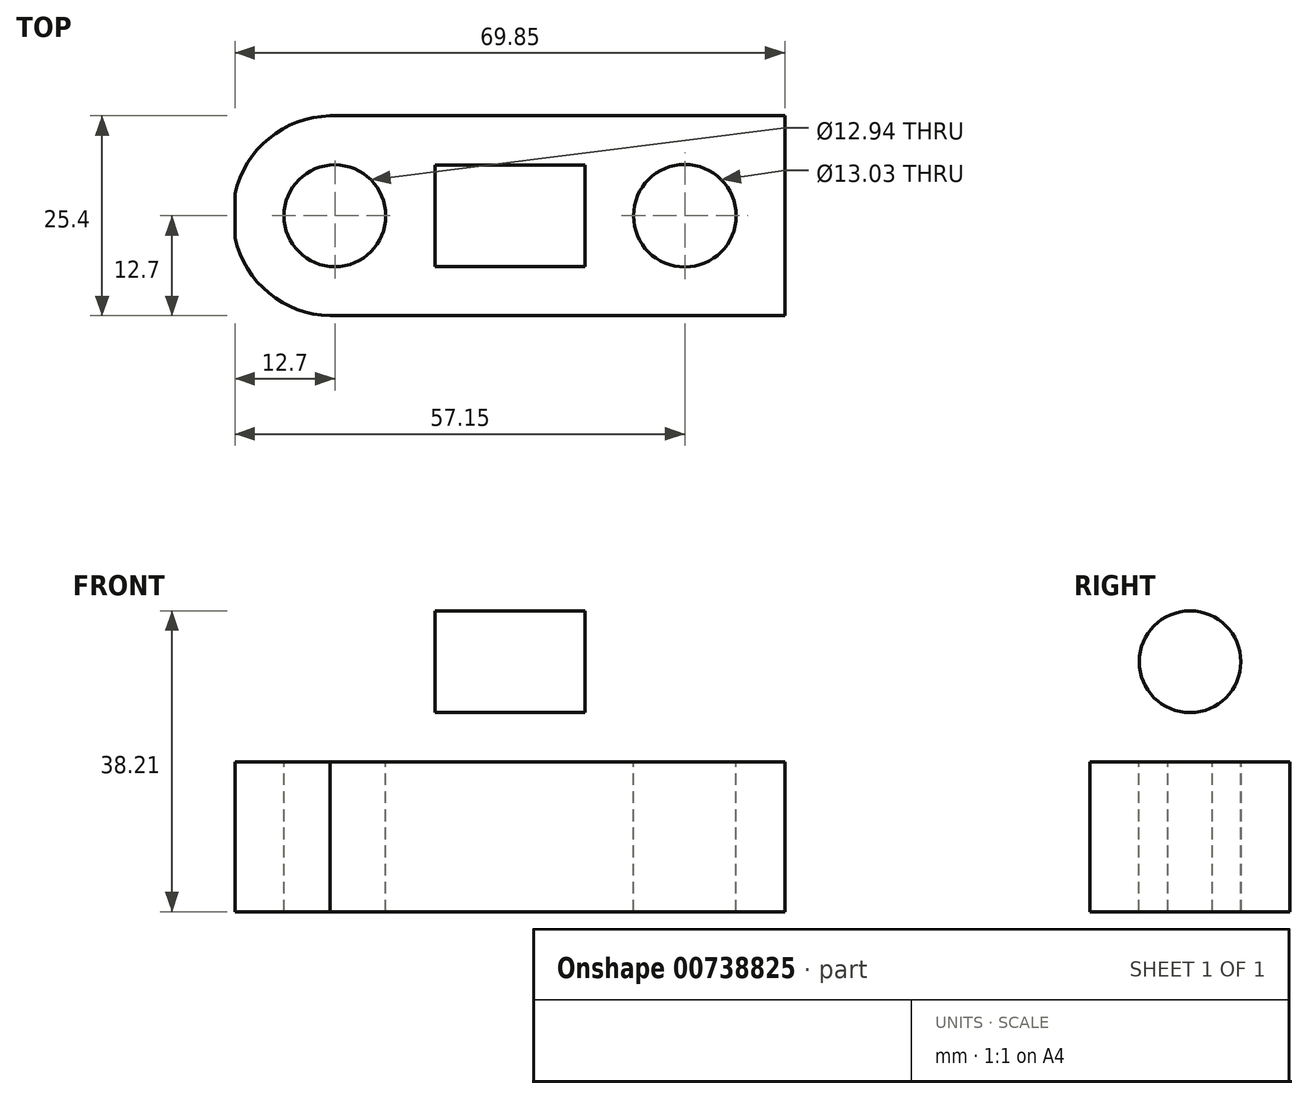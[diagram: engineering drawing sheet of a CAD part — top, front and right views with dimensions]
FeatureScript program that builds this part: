
annotation { "Feature Type Name" : "Feature", "Feature Type Description" : "" }
export const myFeature = defineFeature(function(context is Context, id is Id, definition is map)
    precondition{}
    {
        {
            var Q0;
            Q0=qCreatedBy(makeId("Front.planeOp"),FACE);
            var sketch = newSketch(context, id + "F0", { "sketchPlane" : qUnion([Q0])});
            skLineSegment(sketch, "E0", {"start": v(0, 0) * mm, "end": v(0, 44.45) * mm});
            skLineSegment(sketch, "E1", {"start": v(0, 44.45) * mm, "end": v(69.85, 44.45) * mm});
            skLineSegment(sketch, "E2", {"start": v(69.85, 44.45) * mm, "end": v(69.85, 0) * mm});
            skLineSegment(sketch, "E3", {"start": v(69.85, 0) * mm, "end": v(0, 0) * mm});
            skSolve(sketch);
        }
        {
            var Q0;
            Q0 = qSketchRegion(id + "F0", true);
            extrude(context, id + "F1", {"entities" : qUnion([Q0]), "depth" : 25.4 * mm, "offsetDistance" : 25.4 * mm});
        }
        {
            var Q0;
            Q0=makeQuery(id+"F1.opExtrude","SWEPT_FACE",FACE,{"disambiguationData":[OSD([sQuery(id+"F0.wireOp",EDGE,"E1")])]});
            var sketch = newSketch(context, id + "F2", { "sketchPlane" : qUnion([Q0])});
            skLineSegment(sketch, "E4", {"start": v(25.4, 0) * mm, "end": v(25.4, -25.4) * mm});
            skLineSegment(sketch, "E5", {"start": v(44.45, 0) * mm, "end": v(44.45, -25.4) * mm});
            skSolve(sketch);
        }
        {
            var Q0;
            {var subQ0=sQuery(id+"F2.wireOp",EDGE,"E4");Q0=makeQuery(id+"F2.imprint","IMPRINT",FACE,{"disambiguationData":[TD([[makeQuery(id+"F2.imprint","IMPRINT",EDGE,{"derivedFrom":subQ0}),-1.0]])]});}
            var Q1;
            {var subQ0=sQuery(id+"F2.wireOp",EDGE,"E5");Q1=makeQuery(id+"F2.imprint","IMPRINT",FACE,{"disambiguationData":[TD([[makeQuery(id+"F2.imprint","IMPRINT",EDGE,{"derivedFrom":subQ0}),1.0]])]});}
            extrude(context, id + "F3", {"entities" : qUnion([Q0, Q1]), "operationType" : NewBodyOperationType.REMOVE, "oppositeDirection" : true, "depth" : 25.4 * mm, "offsetDistance" : 25.4 * mm});
        }
        {
            var Q0;
            Q0=makeQuery(id+"F3.boolean.opBoolean","COPY",FACE,{"derivedFrom":makeQuery(id+"F3.opExtrude","CAP_FACE",FACE,{"disambiguationData":[OSD([sQuery(id+"F0.wireOp",EDGE,"E0"),sQuery(id+"F0.wireOp",EDGE,"E1"),sQuery(id+"F2.wireOp",EDGE,"E4")])],"isStart":false})});
            var sketch = newSketch(context, id + "F4", { "sketchPlane" : qUnion([Q0])});
            skLineSegment(sketch, "E6", {"start": v(12.7, 0) * mm, "end": v(12.7, -25.4) * mm});
            skCircle(sketch, "E7", {"center": v(12.7, -12.7) * mm, "radius": 6.47 * mm});
            skArc(sketch, "E8", {"start": v(12.7, 0) * mm, "mid": v(-0.32, -12.7) * mm, "end": v(12.7, -25.4) * mm});
            skSolve(sketch);
        }
        {
            var Q0;
            {var subQ0=sQuery(id+"F4.wireOp",EDGE,"E7");var subQ1=sQuery(id+"F4.wireOp",EDGE,"E6");var subQ2=makeQuery(id+"F4.imprint","INTERSECT",VERTEX,{"disambiguationData":[OD(0.0)],"derivedFrom":[subQ1,subQ0]});Q0=makeQuery(id+"F4.imprint","IMPRINT",FACE,{"disambiguationData":[TD([[makeQuery(id+"F4.imprint","IMPRINT",EDGE,{"disambiguationData":[TD([[subQ2,-1.0]])],"derivedFrom":subQ1}),1.0]])]});}
            var Q1;
            {var subQ0=sQuery(id+"F4.wireOp",EDGE,"E7");var subQ1=sQuery(id+"F4.wireOp",EDGE,"E6");var subQ2=makeQuery(id+"F4.imprint","INTERSECT",VERTEX,{"disambiguationData":[OD(0.0)],"derivedFrom":[subQ1,subQ0]});Q1=makeQuery(id+"F4.imprint","IMPRINT",FACE,{"disambiguationData":[TD([[makeQuery(id+"F4.imprint","IMPRINT",EDGE,{"disambiguationData":[TD([[subQ2,-1.0]])],"derivedFrom":subQ1}),-1.0]])]});}
            var Q2;
            {var subQ0=sQuery(id+"F4.wireOp",EDGE,"E8");var subQ1=sQuery(id+"F0.wireOp",EDGE,"E1");var subQ3=sQuery(id+"F0.wireOp",EDGE,"E0");var subQ6=makeQuery(id+"F3.boolean.opBoolean","COPY",EDGE,{"derivedFrom":makeQuery(id+"F3.opExtrude","CAP_EDGE",EDGE,{"disambiguationData":[OSD([subQ3,subQ1])],"isStart":false})});var subQ7=makeQuery(id+"F4.imprint","INTERSECT",VERTEX,{"disambiguationData":[OD(0.0)],"derivedFrom":[subQ6,subQ0]});Q2=makeQuery(id+"F4.imprint","IMPRINT",FACE,{"disambiguationData":[TD([[makeQuery(id+"F4.imprint","IMPRINT",EDGE,{"disambiguationData":[TD([[subQ7,1.0]])],"derivedFrom":subQ0}),-1.0]])]});}
            var Q3;
            {var subQ0=sQuery(id+"F4.wireOp",EDGE,"E8");var subQ1=sQuery(id+"F0.wireOp",EDGE,"E1");var subQ2=sQuery(id+"F0.wireOp",EDGE,"E0");var subQ3=makeQuery(id+"F3.boolean.opBoolean","COPY",EDGE,{"derivedFrom":makeQuery(id+"F3.opExtrude","CAP_EDGE",EDGE,{"disambiguationData":[OSD([subQ2,subQ1])],"isStart":false})});var subQ4=makeQuery(id+"F4.imprint","INTERSECT",VERTEX,{"disambiguationData":[OD(1.0)],"derivedFrom":[subQ3,subQ0]});Q3=makeQuery(id+"F4.imprint","IMPRINT",FACE,{"disambiguationData":[TD([[makeQuery(id+"F4.imprint","IMPRINT",EDGE,{"disambiguationData":[TD([[subQ4,-1.0]])],"derivedFrom":subQ0}),-1.0]])]});}
            extrude(context, id + "F5", {"entities" : qUnion([Q0, Q1, Q2, Q3]), "operationType" : NewBodyOperationType.REMOVE, "oppositeDirection" : true, "depth" : 25.4 * mm, "offsetDistance" : 25.4 * mm});
        }
        {
            var Q0;
            Q0=makeQuery(id+"F3.boolean.opBoolean","COPY",FACE,{"derivedFrom":makeQuery(id+"F3.opExtrude","CAP_FACE",FACE,{"disambiguationData":[OSD([sQuery(id+"F0.wireOp",EDGE,"E1"),sQuery(id+"F0.wireOp",EDGE,"E2"),sQuery(id+"F2.wireOp",EDGE,"E5")])],"isStart":false})});
            var sketch = newSketch(context, id + "F6", { "sketchPlane" : qUnion([Q0])});
            skLineSegment(sketch, "E9", {"start": v(57.15, 0) * mm, "end": v(57.15, -25.4) * mm});
            skCircle(sketch, "E10", {"center": v(57.15, -12.7) * mm, "radius": 6.51 * mm});
            skArc(sketch, "E11", {"start": v(57.15, -25.4) * mm, "mid": v(70.09, -12.7) * mm, "end": v(57.15, 0) * mm});
            skSolve(sketch);
        }
        {
            var Q0;
            {var subQ0=sQuery(id+"F6.wireOp",EDGE,"E10");var subQ1=sQuery(id+"F6.wireOp",EDGE,"E9");var subQ2=makeQuery(id+"F6.imprint","INTERSECT",VERTEX,{"disambiguationData":[OD(0.0)],"derivedFrom":[subQ1,subQ0]});Q0=makeQuery(id+"F6.imprint","IMPRINT",FACE,{"disambiguationData":[TD([[makeQuery(id+"F6.imprint","IMPRINT",EDGE,{"disambiguationData":[TD([[subQ2,-1.0]])],"derivedFrom":subQ1}),-1.0]])]});}
            var Q1;
            {var subQ0=sQuery(id+"F6.wireOp",EDGE,"E10");var subQ1=sQuery(id+"F6.wireOp",EDGE,"E9");var subQ2=makeQuery(id+"F6.imprint","INTERSECT",VERTEX,{"disambiguationData":[OD(0.0)],"derivedFrom":[subQ1,subQ0]});Q1=makeQuery(id+"F6.imprint","IMPRINT",FACE,{"disambiguationData":[TD([[makeQuery(id+"F6.imprint","IMPRINT",EDGE,{"disambiguationData":[TD([[subQ2,-1.0]])],"derivedFrom":subQ1}),1.0]])]});}
            var Q2;
            {var subQ0=sQuery(id+"F6.wireOp",EDGE,"E11");var subQ1=sQuery(id+"F0.wireOp",EDGE,"E2");var subQ2=sQuery(id+"F0.wireOp",EDGE,"E1");var subQ3=makeQuery(id+"F3.boolean.opBoolean","COPY",EDGE,{"derivedFrom":makeQuery(id+"F3.opExtrude","CAP_EDGE",EDGE,{"disambiguationData":[OSD([subQ2,subQ1])],"isStart":false})});var subQ4=makeQuery(id+"F6.imprint","INTERSECT",VERTEX,{"disambiguationData":[OD(1.0)],"derivedFrom":[subQ3,subQ0]});Q2=makeQuery(id+"F6.imprint","IMPRINT",FACE,{"disambiguationData":[TD([[makeQuery(id+"F6.imprint","IMPRINT",EDGE,{"disambiguationData":[TD([[subQ4,-1.0]])],"derivedFrom":subQ0}),-1.0]])]});}
            var Q3;
            {var subQ0=sQuery(id+"F6.wireOp",EDGE,"E11");var subQ1=sQuery(id+"F0.wireOp",EDGE,"E1");var subQ3=sQuery(id+"F0.wireOp",EDGE,"E2");var subQ6=makeQuery(id+"F3.boolean.opBoolean","COPY",EDGE,{"derivedFrom":makeQuery(id+"F3.opExtrude","CAP_EDGE",EDGE,{"disambiguationData":[OSD([subQ1,subQ3])],"isStart":false})});var subQ7=makeQuery(id+"F6.imprint","INTERSECT",VERTEX,{"disambiguationData":[OD(0.0)],"derivedFrom":[subQ6,subQ0]});Q3=makeQuery(id+"F6.imprint","IMPRINT",FACE,{"disambiguationData":[TD([[makeQuery(id+"F6.imprint","IMPRINT",EDGE,{"disambiguationData":[TD([[subQ7,1.0]])],"derivedFrom":subQ0}),-1.0]])]});}
            extrude(context, id + "F7", {"entities" : qUnion([Q0, Q1, Q2, Q3]), "operationType" : NewBodyOperationType.REMOVE, "oppositeDirection" : true, "depth" : 25.4 * mm, "offsetDistance" : 25.4 * mm});
        }
        {
            var Q0;
            Q0=makeQuery(id+"F3.boolean.opBoolean","COPY",FACE,{"derivedFrom":makeQuery(id+"F3.opExtrude","SWEPT_FACE",FACE,{"disambiguationData":[OSD([sQuery(id+"F2.wireOp",EDGE,"E5")])]})});
            var sketch = newSketch(context, id + "F8", { "sketchPlane" : qUnion([Q0])});
            skLineSegment(sketch, "E12", {"start": v(-25.4, 31.75) * mm, "end": v(0, 31.75) * mm});
            skCircle(sketch, "E13", {"center": v(-12.7, 31.75) * mm, "radius": 6.46 * mm});
            skArc(sketch, "E14", {"start": v(0, 31.75) * mm, "mid": v(-12.7, 44.12) * mm, "end": v(-25.4, 31.75) * mm});
            skSolve(sketch);
        }
        {
            var Q0;
            {var subQ0=sQuery(id+"F8.wireOp",EDGE,"E13");var subQ1=sQuery(id+"F8.wireOp",EDGE,"E12");var subQ2=makeQuery(id+"F8.imprint","INTERSECT",VERTEX,{"disambiguationData":[OD(0.0)],"derivedFrom":[subQ1,subQ0]});Q0=makeQuery(id+"F8.imprint","IMPRINT",FACE,{"disambiguationData":[TD([[makeQuery(id+"F8.imprint","IMPRINT",EDGE,{"disambiguationData":[TD([[subQ2,-1.0]])],"derivedFrom":subQ1}),1.0]])]});}
            var Q1;
            {var subQ0=sQuery(id+"F8.wireOp",EDGE,"E13");var subQ1=sQuery(id+"F8.wireOp",EDGE,"E12");var subQ2=makeQuery(id+"F8.imprint","INTERSECT",VERTEX,{"disambiguationData":[OD(0.0)],"derivedFrom":[subQ1,subQ0]});Q1=makeQuery(id+"F8.imprint","IMPRINT",FACE,{"disambiguationData":[TD([[makeQuery(id+"F8.imprint","IMPRINT",EDGE,{"disambiguationData":[TD([[subQ2,-1.0]])],"derivedFrom":subQ1}),-1.0]])]});}
            var Q2;
            {var subQ0=sQuery(id+"F8.wireOp",EDGE,"E14");Q2=makeQuery(id+"F8.imprint","IMPRINT",FACE,{"disambiguationData":[TD([[makeQuery(id+"F8.imprint","IMPRINT",EDGE,{"derivedFrom":subQ0}),-1.0]])]});}
            extrude(context, id + "F9", {"entities" : qUnion([Q0, Q1, Q2]), "operationType" : NewBodyOperationType.REMOVE, "endBound" : BoundingType.THROUGH_ALL, "oppositeDirection" : true, "depth" : 25.4 * mm, "offsetDistance" : 25.4 * mm});
        }
    });
